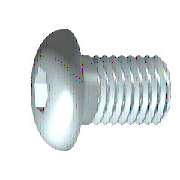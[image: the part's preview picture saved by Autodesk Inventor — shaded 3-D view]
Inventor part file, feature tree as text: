
AUTODESK INVENTOR PART (.ipt)
format: ipt  version: 2012 (Build 160160000, 160)  size: 203,776 bytes
history: native  units: mm (DEFAULTED — no unit token found)
features: extrude x1, plane x1, fillet x1
ambient origin geometry x7: Origin, YZ Plane, XY Plane, X Axis, Y Axis, Z Axis, Center Point
bodies: Solid1 (feature_tree), Body (feature_tree)
feature tree (3):
  extrude  "Slot"  Depth=1.58476mm
  plane  "Work Plane1"
  fillet  "Fillet2"  Radius=1.59014mm
